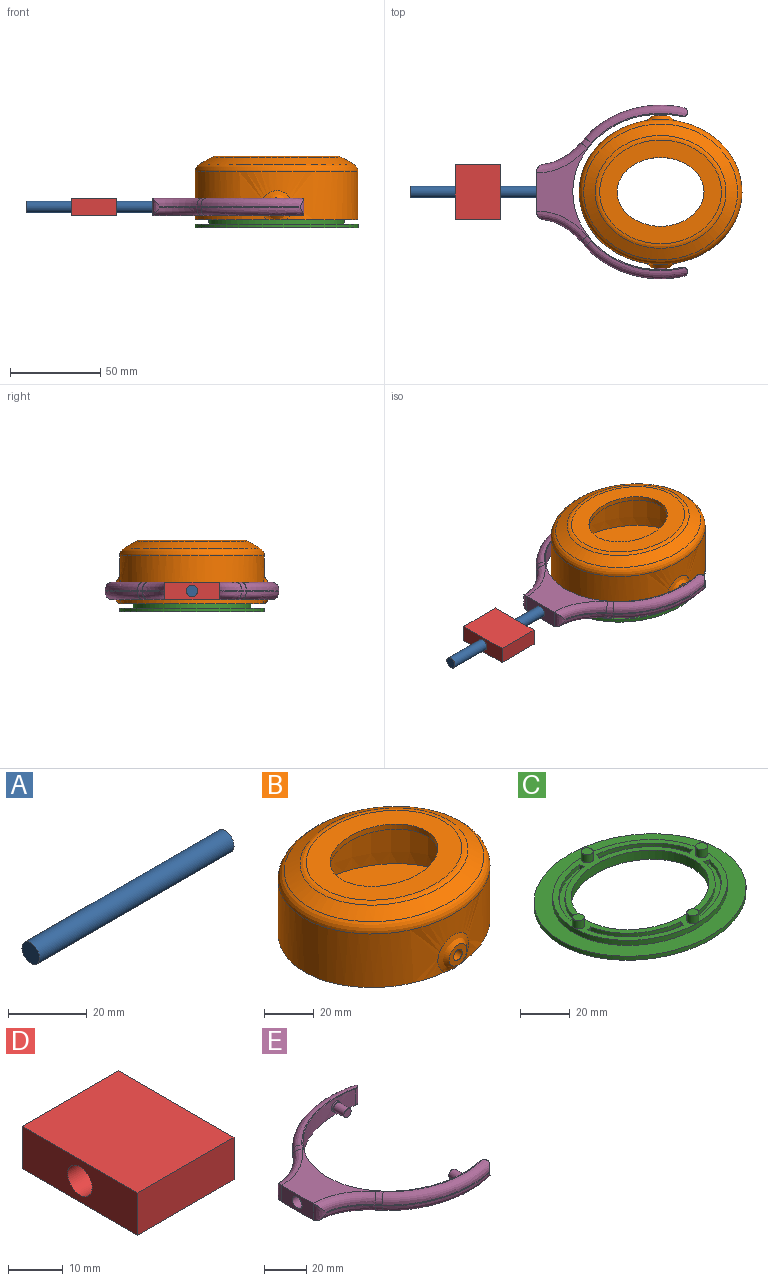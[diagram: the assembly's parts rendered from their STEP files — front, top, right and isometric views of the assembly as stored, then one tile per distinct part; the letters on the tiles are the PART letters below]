
ASSEMBLY  parts=5 mates=4
PART A: 3 faces, bbox 70x6.4x6.4 mm
  f0: cylinder r=3.17mm len=70mm, axis (1,0,0), area 1396.4mm2, adj f1,f2
  f1: plane 6.35x6.35mm, normal (-1,0,0), area 31.7mm2, adj f0
  f2: plane 6.35x6.35mm, normal (1,0,0), area 31.7mm2, adj f0
PART B: 24 faces, bbox 95x89x42 mm
  f0: extruded ~89.65x79.68mm, area 6579.8mm2, adj f4,f6,f22,f23
  f1: extruded ~48x38mm, area 338.9mm2, adj f4,f10
  f2: extruded ~48x38mm, area 338.9mm2, adj f3,f9
  f3: plane 67.33x57.34mm, normal (0,0,1), area 1595.7mm2, adj f2,f7
  f4: plane 90x80.84mm, normal (0,0,-1), area 4148.4mm2, adj f0,f1,f14,f15,f16,f17,f22,f23
  f5: bspline ~84.93x74.96mm, area 1695.7mm2, adj f6,f7
  f6: bspline ~90.01x80.03mm, area 1371mm2, adj f0,f5
  f7: bspline ~72.33x62.35mm, area 534.3mm2, adj f3,f5
  f8: extruded ~84.67x74.7mm, area 5957.8mm2, adj f10,f12,f18,f20
  f9: plane 67.33x57.34mm, normal (0,0,-1), area 1595.7mm2, adj f2,f13
  f10: plane 88.26x78.27mm, normal (0,0,1), area 3495.1mm2, adj f1,f8,f14,f15,f16,f17
  f11: offset ~89.93x79.96mm, area 1638.2mm2, adj f12,f13
  f12: bspline ~85.01x75.02mm, area 651.5mm2, adj f8,f11
  f13: bspline ~69.83x59.85mm, area 261.9mm2, adj f9,f11
  f14: cylinder r=2.5mm len=5mm, axis (0,0,-1), area 39.3mm2, adj f4,f10
  f15: cylinder r=2.5mm len=5mm, axis (0,0,-1), area 39.3mm2, adj f4,f10
  f16: cylinder r=2.5mm len=5mm, axis (0,0,-1), area 39.3mm2, adj f4,f10
  f17: cylinder r=2.5mm len=5mm, axis (0,0,-1), area 39.3mm2, adj f4,f10
  f18: cylinder r=2.5mm len=5mm, axis (0,1,0), area 70.7mm2, adj f8,f19
  f19: plane 10.22x10.22mm, normal (0,-1,0), area 58.9mm2, adj f18,f23
  f20: cylinder r=2.5mm len=5mm, axis (0,-1,0), area 70.7mm2, adj f8,f21
  f21: plane 10.22x10.22mm, normal (0,1,0), area 58.9mm2, adj f20,f22
  f22: bspline ~17.99x17.28mm, area 183mm2, adj f0,f4,f21
  f23: bspline ~17.99x17.28mm, area 183mm2, adj f0,f4,f19
PART C: 34 faces, bbox 90x80x8.5 mm
  f0: plane 75x65mm, normal (0,0,1), area 1002.8mm2, adj f4,f5,f6,f7,f8,f9,f11,f12
  f1: extruded ~90x80mm, area 534.5mm2, adj f2,f3
  f2: plane 90x80mm, normal (0,0,1), area 1826.1mm2, adj f1,f4
  f3: plane 90x80mm, normal (0,0,-1), area 3298.7mm2, adj f1,f5
  f4: extruded ~75x65mm, area 550.5mm2, adj f0,f2
  f5: extruded ~60x50mm, area 779.2mm2, adj f0,f3
  f6: extruded ~28.08x23.29mm, area 78.2mm2, adj f0,f7,f8,f10
  f7: cylinder r=4.9mm len=2.38mm, axis (0,0,-1), area 5.1mm2, adj f0,f6,f9,f10
  f8: cylinder r=4.9mm len=2.42mm, axis (0,0,-1), area 5.2mm2, adj f0,f6,f9,f10
  f9: extruded ~29.64x24.83mm, area 82.6mm2, adj f0,f7,f8,f10
  f10: plane 30.47x25.73mm, normal (0,0,1), area 99.4mm2, adj f6,f7,f8,f9
  f11: cylinder r=4.9mm len=2.42mm, axis (0,0,-1), area 5.2mm2, adj f0,f12,f14,f15
  f12: extruded ~28.08x23.29mm, area 78.2mm2, adj f0,f11,f13,f15
  f13: cylinder r=4.9mm len=2.38mm, axis (0,0,-1), area 5.1mm2, adj f0,f12,f14,f15
  f14: extruded ~29.64x24.83mm, area 82.6mm2, adj f0,f11,f13,f15
  f15: plane 30.47x25.72mm, normal (0,0,1), area 99.4mm2, adj f11,f12,f13,f14
  f16: cylinder r=4.9mm len=2.42mm, axis (0,0,-1), area 5.2mm2, adj f0,f17,f18,f19
  f17: extruded ~28.08x23.29mm, area 78.2mm2, adj f0,f16,f18,f20
  f18: plane 30.47x25.73mm, normal (0,0,1), area 99.4mm2, adj f16,f17,f19,f20
  f19: extruded ~29.64x24.83mm, area 82.6mm2, adj f0,f16,f18,f20
  f20: cylinder r=4.9mm len=2.38mm, axis (0,0,-1), area 5.1mm2, adj f0,f17,f18,f19
  f21: cylinder r=4.9mm len=2.42mm, axis (0,0,-1), area 5.2mm2, adj f0,f22,f24,f25
  f22: extruded ~28.08x23.29mm, area 78.2mm2, adj f0,f21,f23,f25
  f23: cylinder r=4.9mm len=2.38mm, axis (0,0,-1), area 5.1mm2, adj f0,f22,f24,f25
  f24: extruded ~29.64x24.83mm, area 82.6mm2, adj f0,f21,f23,f25
  f25: plane 30.47x25.72mm, normal (0,0,1), area 99.4mm2, adj f21,f22,f23,f24
  f26: plane 4.8x4.8mm, normal (0,0,1), area 18.1mm2, adj f27
  f27: cylinder r=2.4mm len=4.8mm, axis (0,0,-1), area 60.3mm2, adj f0,f26
  f28: plane 4.8x4.8mm, normal (0,0,1), area 18.1mm2, adj f29
  f29: cylinder r=2.4mm len=4.8mm, axis (0,0,-1), area 60.3mm2, adj f0,f28
  f30: plane 4.8x4.8mm, normal (0,0,1), area 18.1mm2, adj f31
  f31: cylinder r=2.4mm len=4.8mm, axis (0,0,-1), area 60.3mm2, adj f0,f30
  f32: plane 4.8x4.8mm, normal (0,0,1), area 18.1mm2, adj f33
  f33: cylinder r=2.4mm len=4.8mm, axis (0,0,-1), area 60.3mm2, adj f0,f32
PART D: 7 faces, bbox 25x30x9.5 mm
  f0: plane 30x25mm, normal (0,0,-1), area 750mm2, adj f1,f4,f5,f6
  f1: plane 25x9.5mm, normal (0,-1,0), area 237.5mm2, adj f0,f2,f5,f6
  f2: plane 30x25mm, normal (0,0,1), area 750mm2, adj f1,f4,f5,f6
  f3: cylinder r=3.17mm len=25mm, axis (1,0,0), area 498.7mm2, adj f5,f6
  f4: plane 25x9.5mm, normal (0,1,0), area 237.5mm2, adj f0,f2,f5,f6
  f5: plane 30x9.5mm, normal (-1,0,0), area 253.3mm2, adj f0,f1,f2,f3,f4
  f6: plane 30x9.5mm, normal (1,0,0), area 253.3mm2, adj f0,f1,f2,f3,f4
PART E: 38 faces, bbox 86.6x96.3x10.6 mm
  f0: cylinder r=2.75mm len=5.5mm, axis (0,1,0), area 17.3mm2, adj f3,f4
  f1: cylinder r=2.4mm len=7mm, axis (0,-1,0), area 105.6mm2, adj f2,f3
  f2: plane 4.8x4.8mm, normal (0,1,0), area 18.1mm2, adj f1
  f3: plane 5.5x5.5mm, normal (0,1,0), area 5.7mm2, adj f0,f1
  f4: extruded ~85.98x60.33mm, area 1545.8mm2, adj f0,f5,f16,f17,f21,f22
  f5: cylinder r=2.75mm len=5.5mm, axis (0,-1,0), area 17.3mm2, adj f4,f8
  f6: cylinder r=2.4mm len=7mm, axis (0,1,0), area 105.6mm2, adj f7,f8
  f7: plane 4.8x4.8mm, normal (0,-1,0), area 18.1mm2, adj f6
  f8: plane 5.5x5.5mm, normal (0,-1,0), area 5.7mm2, adj f5,f6
  f9: extruded ~54.73x18mm, area 30mm2, adj f10,f20,f31,f37
  f10: extruded ~2.65x2.2mm, area 1.7mm2, adj f9,f11,f32,f36
  f11: extruded ~20.64x12.09mm, area 12.2mm2, adj f10,f33,f34,f35
  f12: plane 21.61x9.5mm, normal (-1,0,0), area 173.6mm2, adj f16,f17,f18,f26,f27,f28,f33,f34
  f13: extruded ~20.64x12.09mm, area 12.2mm2, adj f14,f26,f27,f28
  f14: extruded ~2.65x2.2mm, area 1.7mm2, adj f13,f15,f25,f29
  f15: extruded ~54.73x18mm, area 30mm2, adj f14,f23,f24,f30
  f16: plane 87.29x82.05mm, normal (0,0,1), area 635.7mm2, adj f4,f12,f21,f22,f24,f25,f26,f31
  f17: plane 87.29x82.05mm, normal (0,0,-1), area 635.7mm2, adj f4,f12,f21,f22,f28,f29,f30,f35
  f18: cylinder r=3.17mm len=10mm, axis (-1,0,0), area 199.5mm2, adj f12,f19
  f19: plane 6.35x6.35mm, normal (-1,0,0), area 31.7mm2, adj f18
  f20: cylinder r=2.6mm len=8.38mm, axis (0,0,-1), area 18mm2, adj f9,f21,f31,f37
  f21: cylinder r=2.6mm len=9.5mm, axis (0,0,-1), area 41.6mm2, adj f4,f16,f17,f20,f31,f37
  f22: cylinder r=2.6mm len=9.5mm, axis (0,0,-1), area 41.6mm2, adj f4,f16,f17,f23,f24,f30
  f23: cylinder r=2.6mm len=8.38mm, axis (0,0,-1), area 18mm2, adj f15,f22,f24,f30
  f24: bspline ~60.75x22.71mm, area 437.3mm2, adj f15,f16,f22,f23,f25
  f25: bspline ~5.86x5.78mm, area 25.4mm2, adj f14,f16,f24,f26
  f26: bspline ~28.41x16.85mm, area 207.2mm2, adj f12,f13,f16,f25,f27
  f27: bspline ~10.45x4.46mm, area 42.7mm2, adj f12,f13,f26,f28
  f28: bspline ~28.41x16.85mm, area 207.2mm2, adj f12,f13,f17,f27,f29
  f29: bspline ~5.86x5.78mm, area 25.4mm2, adj f14,f17,f28,f30
  f30: bspline ~60.75x22.71mm, area 437.3mm2, adj f15,f17,f22,f23,f29
  f31: bspline ~60.75x22.71mm, area 437.3mm2, adj f9,f16,f20,f21,f32
  f32: bspline ~5.86x5.78mm, area 25.4mm2, adj f10,f16,f31,f33
  f33: bspline ~28.41x16.85mm, area 207.2mm2, adj f11,f12,f16,f32,f34
  f34: bspline ~10.45x4.46mm, area 42.8mm2, adj f11,f12,f33,f35
  f35: bspline ~28.41x16.85mm, area 207.1mm2, adj f11,f12,f17,f34,f36
  f36: bspline ~5.86x5.78mm, area 25.4mm2, adj f10,f17,f35,f37
  f37: bspline ~60.75x22.71mm, area 437.3mm2, adj f9,f17,f20,f21,f36
PLACE A t=(-10,0,0)mm
PLACE B at identity
PLACE C at identity
PLACE D t=(14.98,0,0)mm
PLACE E at identity
MATE fastened C.f16 <-> B.f14  axis (0,0,1) through (0,-30,4.5)mm
MATE slider D.f3 <-> A.f0  axis (-1,0,0) through (-113.52,0,11.5)mm
MATE cylindrical A.f0 <-> E.f18  axis (1,0,0) through (-68.5,0,11.5)mm
MATE revolute E.f0 <-> B.f18  axis (0,1,0) through (0,-42,11.5)mm
